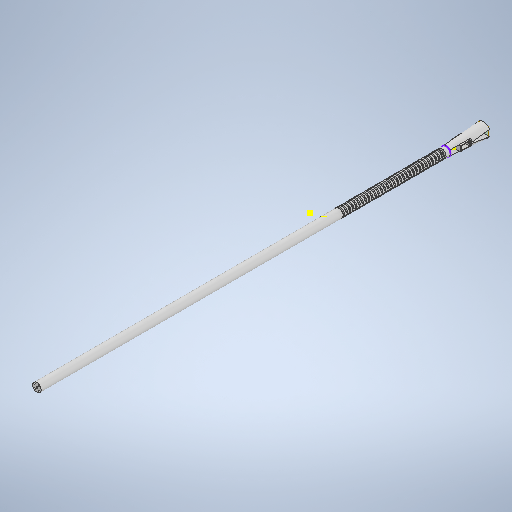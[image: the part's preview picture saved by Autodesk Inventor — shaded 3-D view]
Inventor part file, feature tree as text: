
AUTODESK INVENTOR PART (.ipt)
format: ipt  version: 2025.2 (Build 292293000, 293)  size: 913,408 bytes
history: native  units: mm
features: sketch x31, extrude x20, plane x5, loft x1, other x1
ambient origin geometry x8: Origin, YZ Plane, XZ Plane, XY Plane, X Axis, Y Axis, Z Axis, Center Point
bodies: Solid1 (feature_tree)
feature tree (58):
  extrude  "Extrusion1"  Depth=40.0mm TaperAngle=0.0deg
  plane  "Work Plane1"
  extrude  "Extrusion2"  Depth=1.3mm
  extrude  "Extrusion3"  Depth=0.5mm
  extrude  "Extrusion4"  Depth=40.0mm
  sketch  "Sketch5"  dims[d11=0.3mm d12=0.3mm]
  extrude  "Extrusion5"  Depth=0.3mm
  extrude  "Extrusion6"  Depth=0.3mm
  extrude  "Extrusion7"  Depth=0.6mm
  extrude  "Extrusion8"  Depth=0.6mm
  plane  "Work Plane2"
  extrude  "Extrusion9"  Depth=40.0mm TaperAngle=360.0deg
  extrude  "Extrusion10"  Depth=0.6mm TaperAngle=0.0deg
  sketch  "Sketch12"  dims[d39=4.0mm d40=0.1mm]
  sketch  "Sketch13"  dims[d41=20.75mm d42=0.0mm d43=0.2mm]
  extrude  "Extrusion11"  Depth=0.6mm TaperAngle=0.0deg
  sketch  "Sketch16"  dims[d48=0.25mm d51=0.75mm]
  sketch  "Sketch17"  dims[d52=0.2mm d53=0.2mm]
  sketch  "Sketch18"  dims[d54=2.591063mm d55=0.5mm]
  extrude  "Extrusion13"  [1 undecoded]
  extrude  "Extrusion14"  Depth=0.1mm
  extrude  "Extrusion18"  Depth=0.2mm
  extrude  "Extrusion19"  Depth=2.0mm
  extrude  "Extrusion20"  Depth=0.75mm
  plane  "Work Plane3"
  sketch  "Sketch38"  dims[d67=1.0mm]
  sketch  "Sketch39"  dims[d68=1.0mm]
  loft  "Loft3"
  plane  "Work Plane4"
  extrude  "Extrusion21"  Depth=0.5mm
  sketch  "Sketch43"  dims[d71=4.0mm d72=0.0mm]
  extrude  "Extrusion23"  Depth=0.2mm
  sketch  "Sketch48"  dims[d93=8.0mm d94=0.0mm]
  sketch  "Sketch49"  dims[d95=1.5mm d96=0.0mm]
  plane  "Work Plane5"
  extrude  "Extrusion24"  Depth=2.5mm
  extrude  "Extrusion25"  Depth=20.754mm TaperAngle=0.0deg
  sketch  "Sketch1"  dims[d0=3.0mm d1=40.0mm d2=0.0mm]
  sketch  "Sketch2"  dims[d5=0.5mm d6=0.5mm]
  sketch  "Sketch3"  dims[d7=0.6mm d8=40.0mm]
  sketch  "Sketch4"  dims[d9=0.3mm d10=0.3mm]
  sketch  "Sketch Circular Pattern1"  dims[d3=-40.0mm d4=1.3mm]
  sketch  "Sketch6"  dims[d13=54.75mm d14=5.0mm d15=0.0mm d16=0.0mm d17=0.6mm]
  sketch  "Sketch7"  dims[d20=54.75mm d21=0.0mm d22=0.6mm]
  sketch  "Sketch8"  dims[d23=2.3mm d24=40.0mm d26=360.0deg]
  sketch  "Sketch9"  dims[d28=54.75mm d29=0.0mm d30=0.6mm d31=0.0mm]
  sketch  "Sketch10"  dims[d32=0.6mm d33=0.0mm d34=0.6mm d35=0.0mm]
  sketch  "Sketch11"  dims[d36=10.0mm d37=0.0mm d38=-13.25mm]
  sketch  "Sketch14"  dims[d44=0.5mm d45=2.0mm]
  sketch  "Sketch19"  dims[d56=0.1mm d57=0.2mm]
  sketch  "Sketch21"  dims[d58=0.25mm d59=2.5mm]
  sketch  "Sketch36"  dims[d60=2.5mm d61=20.754mm d62=0.0mm]
  sketch  "Sketch37"  dims[d63=46.004mm d64=0.0mm]
  other  "Edges3"
  sketch  "Sketch40"  dims[d69=99.0mm d70=0.0mm]
  sketch  "Sketch44"  dims[d74=4.5mm]
  sketch  "Sketch50"  dims[d97=0.6mm]
  sketch  "Sketch51"  dims[d98=1.5mm d99=0.0mm d100=55.0mm d101=4.75mm d102=0.0mm d103=90.0deg d104=0.0mm d105=90.0deg d106=-5.0mm d107=2.25mm d108=7.0mm d109=13.75mm d110=0.0mm d128=100.0mm d129=0.0mm d130=0.25mm d133=-1.75mm d134=0.3mm d136=0.3mm d137=0.3mm d138=0.3mm d139=0.3mm d140=0.3mm d141=0.15mm d142=0.15mm d143=3.5mm d144=0.0mm d145=0.4mm d146=0.2mm d147=0.2mm d148=3.407915mm d149=0.02618mm d150=145.25mm d151=0.0mm d73=0.5mm d79=0.5mm d80=0.872665mm d81=0.5mm d82=0.872665mm d91=0.5mm d92=0.872665mm d126=0.5mm d127=0.872665mm]
note: 1 required parameter value undecoded (feature->parameter linkage not recoverable at this tier; creation-order binding heuristic only, values carry confidence <= 0.55)
